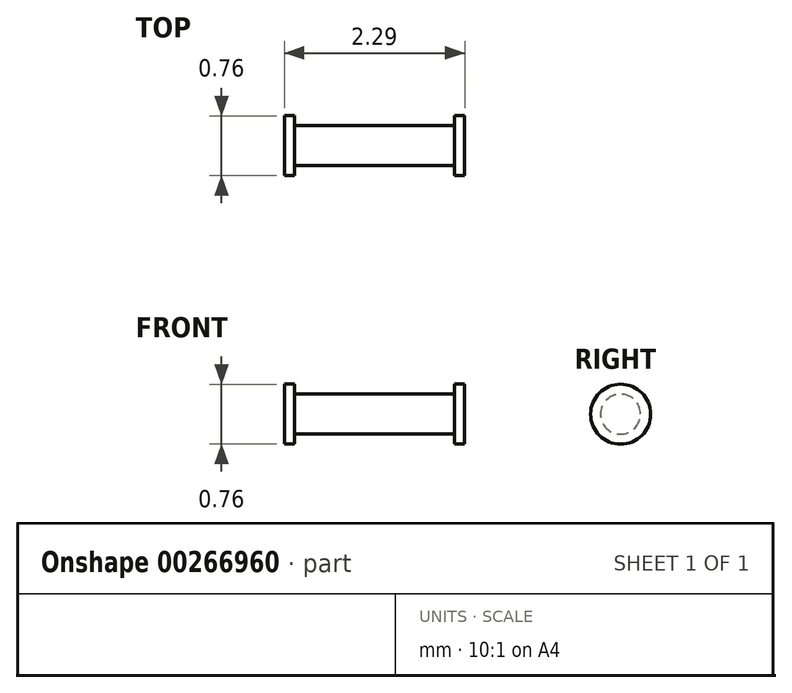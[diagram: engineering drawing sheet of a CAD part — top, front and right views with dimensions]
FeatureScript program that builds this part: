
annotation { "Feature Type Name" : "Feature", "Feature Type Description" : "" }
export const myFeature = defineFeature(function(context is Context, id is Id, definition is map)
    precondition{}
    {
        {
            var Q0;
            Q0=qCreatedBy(makeId("Front.planeOp"),FACE);
            var sketch = newSketch(context, id + "F0", { "sketchPlane" : qUnion([Q0])});
            skLineSegment(sketch, "E0", {"start": v(2.29, 0) * mm, "end": v(0, 0) * mm});
            skLineSegment(sketch, "E1", {"start": v(0, 0) * mm, "end": v(0, 0.38) * mm});
            skLineSegment(sketch, "E2", {"start": v(0, 0.38) * mm, "end": v(0.13, 0.38) * mm});
            skLineSegment(sketch, "E3", {"start": v(0.13, 0.38) * mm, "end": v(0.13, 0.25) * mm});
            skLineSegment(sketch, "E4", {"start": v(0.13, 0.25) * mm, "end": v(2.16, 0.25) * mm});
            skLineSegment(sketch, "E5", {"start": v(2.16, 0.25) * mm, "end": v(2.16, 0.38) * mm});
            skLineSegment(sketch, "E6", {"start": v(2.16, 0.38) * mm, "end": v(2.29, 0.38) * mm});
            skLineSegment(sketch, "E7", {"start": v(2.29, 0.38) * mm, "end": v(2.29, 0) * mm});
            skSolve(sketch);
        }
        {
            var Q0;
            Q0 = qSketchRegion(id + "F0", true);
            var Q1;
            Q1=sQuery(id+"F0.wireOp",EDGE,"E0");
            revolve(context, id + "F1", {"entities" : qUnion([Q0]), "axis" : qUnion([Q1]), "revolveType" : RevolveType.FULL});
        }
    });
